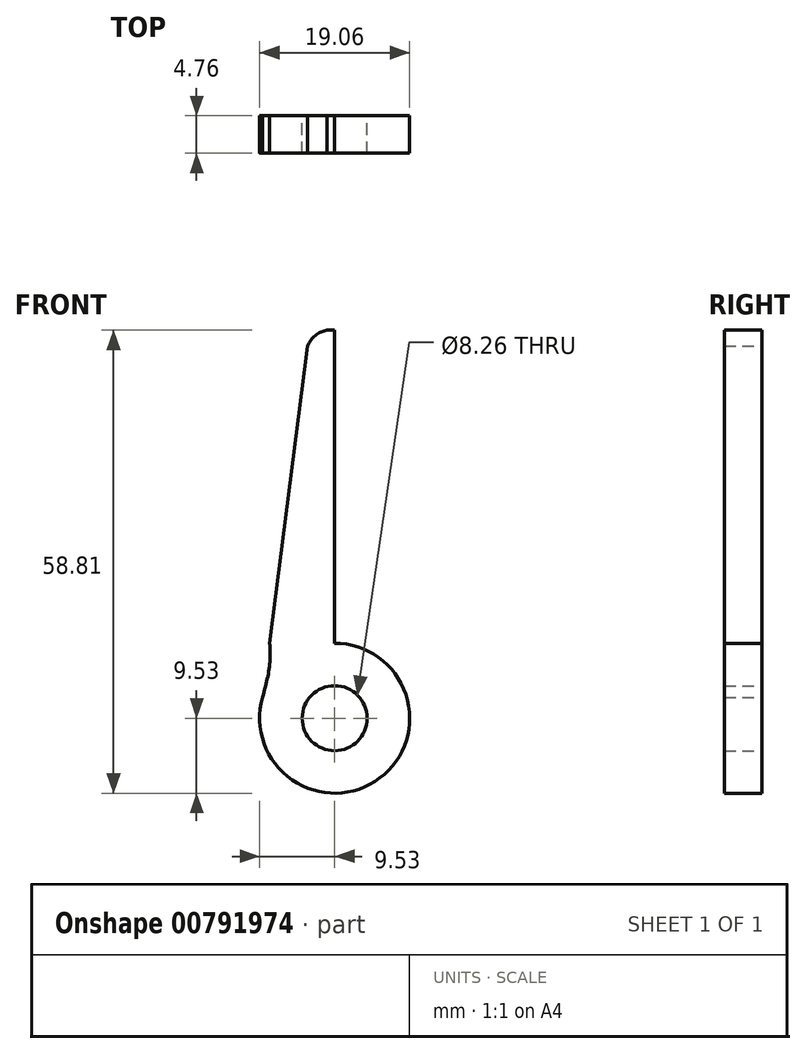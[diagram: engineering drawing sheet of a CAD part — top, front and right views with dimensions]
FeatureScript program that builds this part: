
annotation { "Feature Type Name" : "Feature", "Feature Type Description" : "" }
export const myFeature = defineFeature(function(context is Context, id is Id, definition is map)
    precondition{}
    {
        {
            var Q0;
            Q0=qCreatedBy(makeId("Front.planeOp"),FACE);
            var sketch = newSketch(context, id + "F0", { "sketchPlane" : qUnion([Q0])});
            skCircle(sketch, "E0", {"center": v(0, 0) * mm, "radius": 9.53 * mm});
            skCircle(sketch, "E1", {"center": v(0, 0) * mm, "radius": 4.13 * mm});
            skLineSegment(sketch, "E2.bottom", {"start": v(0, 9.53) * mm, "end": v(-8.26, 9.53) * mm});
            skLineSegment(sketch, "E2.top", {"start": v(0, 49.28) * mm, "end": v(-8.26, 49.28) * mm});
            skLineSegment(sketch, "E2.left", {"start": v(0, 9.53) * mm, "end": v(0, 49.28) * mm});
            skLineSegment(sketch, "E2.right", {"start": v(-8.26, 9.53) * mm, "end": v(-8.26, 49.28) * mm});
            skFitSpline(sketch, "E3", {"points": [v(-8.26, 9.53) * mm, v(-8.26, 6.8) * mm, v(-9.15, 2.65) * mm], "startDerivative": vector(0.36, -5.82) * mm, "endDerivative": vector(-2.04, -7.86) * mm});
            skLineSegment(sketch, "E4", {"start": v(-8.25, 9.53) * mm, "end": v(-3.18, 49.28) * mm});
            skArc(sketch, "E5", {"start": v(0, 49.28) * mm, "mid": v(-2.69, 48.42) * mm, "end": v(-3.63, 45.76) * mm});
            skSolve(sketch);
        }
        {
            var Q0;
            {var subQ1=sQuery(id+"F0.wireOp",EDGE,"E2.bottom");Q0=makeQuery(id+"F0.imprint","IMPRINT",FACE,{"disambiguationData":[TD([[makeQuery(id+"F0.imprint","IMPRINT",EDGE,{"derivedFrom":subQ1}),-1.0]])]});}
            var Q1;
            Q1=makeQuery(id+"F0.imprint","IMPRINT",FACE,{"disambiguationData":[TD([[makeQuery(id+"F0.imprint","IMPRINT",EDGE,{"derivedFrom":sQuery(id+"F0.wireOp",EDGE,"E1")}),-1.0]])]});
            var Q2;
            {var subQ0=sQuery(id+"F0.wireOp",EDGE,"E2.bottom");Q2=makeQuery(id+"F0.imprint","IMPRINT",FACE,{"disambiguationData":[TD([[makeQuery(id+"F0.imprint","IMPRINT",EDGE,{"derivedFrom":subQ0}),1.0]])]});}
            extrude(context, id + "F1", {"entities" : qUnion([Q0, Q1, Q2]), "depth" : 4.76 * mm, "offsetDistance" : 25.4 * mm});
        }
    });
